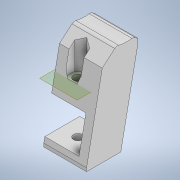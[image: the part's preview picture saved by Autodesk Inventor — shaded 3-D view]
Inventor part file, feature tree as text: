
AUTODESK INVENTOR PART (.ipt)
format: ipt  version: 2020 (Build 240168000, 168)  size: 180,736 bytes
history: native  units: in
note: dims shown in document units (in); Inventor stores cm internally (conversion verified against a paired STEP export)
features: extrude x6, sketch x6, fillet x2, plane x1, chamfer x1
ambient origin geometry x8: Origin, YZ Plane, XZ Plane, XY Plane, X Axis, Y Axis, Z Axis, Center Point
bodies: Solid1 (feature_tree)
feature tree (16):
  extrude  "Extrusion1"  Depth=1.25in
  extrude  "Extrusion2"  Depth=0.25in
  extrude  "Extrusion3"  Depth=1.0in
  extrude  "Extrusion4"  TaperAngle=0.0deg  [1 undecoded]
  plane  "Work Plane1"
  extrude  "Extrusion5"  Depth=0.75in
  fillet  "Fillet1"  [1 undecoded]
  chamfer  "Chamfer1"  Distance=0.5in
  fillet  "Fillet2"  Radius=0.2656in
  extrude  "Extrusion6"  TaperAngle=0.0deg  [1 undecoded]
  sketch  "Sketch1"  dims[d0=1.25in d1=2.75in]
  sketch  "Sketch2"  dims[d2=1.5in d3=0.0in d4=0.25in]
  sketch  "Sketch3"  dims[d5=0.25in d6=1.0in]
  sketch  "Sketch4"  dims[d7=1.0in d8=0.0in d9=0.0in]
  sketch  "Sketch5"  dims[d10=0.625in d11=0.75in d12=0.0in d13=0.0in]
  sketch  "Sketch6"  dims[d14=0.5in d15=0.5in d16=0.2656in d17=0.0in d18=0.0in d19=-0.5in d20=0.4375in d21=1.5in d22=0.0in d23=1.0in d24=0.125in d25=0.125in d26=0.125in d27=45.0deg d28=0.125in d29=2.5in d30=0.5in d31=0.0in d32=0.0in d33=1.0in]
note: 3 required parameter values undecoded (feature->parameter linkage not recoverable at this tier; creation-order binding heuristic only, values carry confidence <= 0.55)
